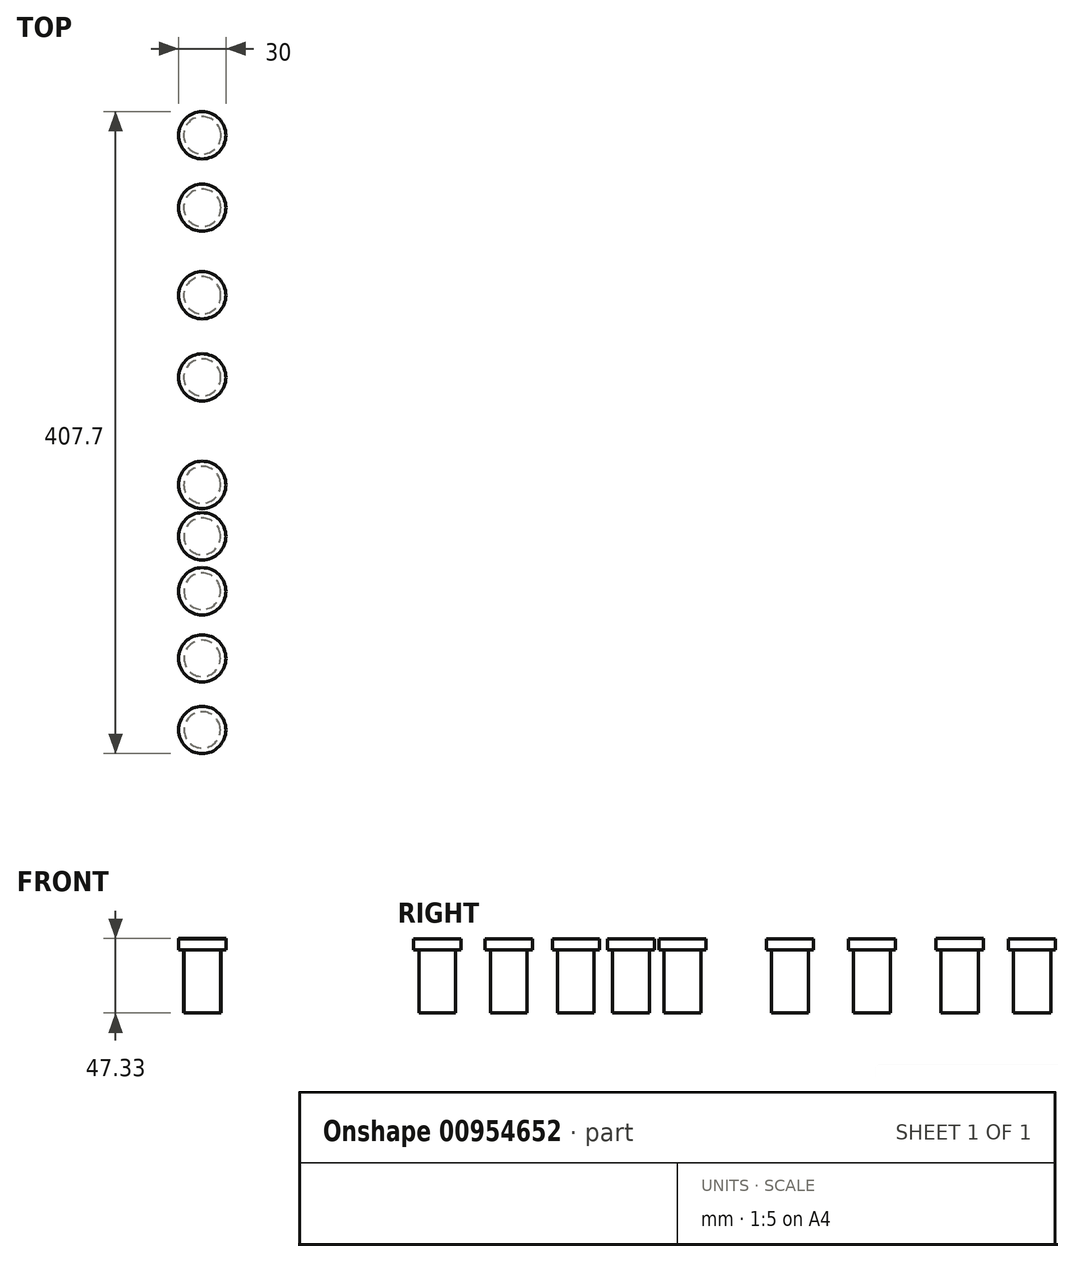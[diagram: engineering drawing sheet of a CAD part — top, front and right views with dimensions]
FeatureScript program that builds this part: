
annotation { "Feature Type Name" : "Feature", "Feature Type Description" : "" }
export const myFeature = defineFeature(function(context is Context, id is Id, definition is map)
    precondition{}
    {
        {
            var Q0;
            Q0=qCreatedBy(makeId("Right.planeOp"),FACE);
            var sketch = newSketch(context, id + "F0", { "sketchPlane" : qUnion([Q0])});
            skLineSegment(sketch, "E0.bottom", {"start": v(0, 0) * mm, "end": v(11.7, 0) * mm});
            skLineSegment(sketch, "E0.top", {"start": v(0, 47) * mm, "end": v(11.7, 47) * mm});
            skLineSegment(sketch, "E0.left", {"start": v(0, 0) * mm, "end": v(0, 47) * mm});
            skLineSegment(sketch, "E0.right", {"start": v(11.7, 0) * mm, "end": v(11.7, 47) * mm});
            skLineSegment(sketch, "E1.bottom", {"start": v(0, 47) * mm, "end": v(15, 47) * mm});
            skLineSegment(sketch, "E1.top", {"start": v(0, 40) * mm, "end": v(15, 40) * mm});
            skLineSegment(sketch, "E1.left", {"start": v(0, 40) * mm, "end": v(0, 47) * mm});
            skLineSegment(sketch, "E1.right", {"start": v(15, 40) * mm, "end": v(15, 47) * mm});
            skLineSegment(sketch, "E2", {"start": v(-171.22, 0) * mm, "end": v(221.99, 0) * mm, "construction": true});
            skLineSegment(sketch, "E3.bottom", {"start": v(-67.64, 0) * mm, "end": v(-79.24, 0) * mm});
            skLineSegment(sketch, "E3.top", {"start": v(-67.64, 40) * mm, "end": v(-79.24, 40) * mm});
            skLineSegment(sketch, "E3.left", {"start": v(-67.64, 0) * mm, "end": v(-67.64, 40) * mm});
            skLineSegment(sketch, "E3.right", {"start": v(-79.24, 0) * mm, "end": v(-79.24, 40) * mm});
            skLineSegment(sketch, "E4.bottom", {"start": v(-67.64, 40) * mm, "end": v(-82.64, 40) * mm});
            skLineSegment(sketch, "E4.top", {"start": v(-67.64, 47) * mm, "end": v(-82.64, 47) * mm});
            skLineSegment(sketch, "E4.left", {"start": v(-67.64, 40) * mm, "end": v(-67.64, 47) * mm});
            skLineSegment(sketch, "E4.right", {"start": v(-82.64, 40) * mm, "end": v(-82.64, 47) * mm});
            skLineSegment(sketch, "E5.bottom", {"start": v(-110.27, 0) * mm, "end": v(-121.82, 0) * mm});
            skLineSegment(sketch, "E5.top", {"start": v(-110.27, 40) * mm, "end": v(-121.82, 40) * mm});
            skLineSegment(sketch, "E5.left", {"start": v(-110.27, 0) * mm, "end": v(-110.27, 40) * mm});
            skLineSegment(sketch, "E5.right", {"start": v(-121.82, 0) * mm, "end": v(-121.82, 40) * mm});
            skLineSegment(sketch, "E6.bottom", {"start": v(-110.27, 40) * mm, "end": v(-125.27, 40) * mm});
            skLineSegment(sketch, "E6.top", {"start": v(-110.27, 47) * mm, "end": v(-125.27, 47) * mm});
            skLineSegment(sketch, "E6.left", {"start": v(-110.27, 40) * mm, "end": v(-110.27, 47) * mm});
            skLineSegment(sketch, "E6.right", {"start": v(-125.27, 40) * mm, "end": v(-125.27, 47) * mm});
            skLineSegment(sketch, "E7.bottom", {"start": v(-155.71, 0) * mm, "end": v(-167.21, 0) * mm});
            skLineSegment(sketch, "E7.top", {"start": v(-155.71, 40) * mm, "end": v(-167.21, 40) * mm});
            skLineSegment(sketch, "E7.left", {"start": v(-155.71, 0) * mm, "end": v(-155.71, 40) * mm});
            skLineSegment(sketch, "E7.right", {"start": v(-167.21, 0) * mm, "end": v(-167.21, 40) * mm});
            skLineSegment(sketch, "E8.bottom", {"start": v(-155.71, 40) * mm, "end": v(-170.71, 40) * mm});
            skLineSegment(sketch, "E8.top", {"start": v(-155.71, 47) * mm, "end": v(-170.71, 47) * mm});
            skLineSegment(sketch, "E8.left", {"start": v(-155.71, 40) * mm, "end": v(-155.71, 47) * mm});
            skLineSegment(sketch, "E8.right", {"start": v(-170.71, 40) * mm, "end": v(-170.71, 47) * mm});
            skLineSegment(sketch, "E9.bottom", {"start": v(221.99, 0) * mm, "end": v(210.09, 0) * mm});
            skLineSegment(sketch, "E9.top", {"start": v(221.99, 40) * mm, "end": v(210.09, 40) * mm});
            skLineSegment(sketch, "E9.left", {"start": v(221.99, 0) * mm, "end": v(221.99, 40) * mm});
            skLineSegment(sketch, "E9.right", {"start": v(210.09, 0) * mm, "end": v(210.09, 40) * mm});
            skLineSegment(sketch, "E10.bottom", {"start": v(221.99, 40) * mm, "end": v(206.99, 40) * mm});
            skLineSegment(sketch, "E10.top", {"start": v(221.99, 47) * mm, "end": v(206.99, 47) * mm});
            skLineSegment(sketch, "E10.left", {"start": v(221.99, 40) * mm, "end": v(221.99, 47) * mm});
            skLineSegment(sketch, "E10.right", {"start": v(206.99, 40) * mm, "end": v(206.99, 47) * mm});
            skLineSegment(sketch, "E11.bottom", {"start": v(120.39, 0) * mm, "end": v(108.59, 0) * mm});
            skLineSegment(sketch, "E11.top", {"start": v(120.39, 40) * mm, "end": v(108.59, 40) * mm});
            skLineSegment(sketch, "E11.left", {"start": v(120.39, 0) * mm, "end": v(120.39, 40) * mm});
            skLineSegment(sketch, "E11.right", {"start": v(108.59, 0) * mm, "end": v(108.59, 40) * mm});
            skLineSegment(sketch, "E12.bottom", {"start": v(120.39, 40) * mm, "end": v(105.39, 40) * mm});
            skLineSegment(sketch, "E12.top", {"start": v(120.39, 47) * mm, "end": v(105.39, 47) * mm});
            skLineSegment(sketch, "E12.left", {"start": v(120.39, 40) * mm, "end": v(120.39, 47) * mm});
            skLineSegment(sketch, "E12.right", {"start": v(105.39, 40) * mm, "end": v(105.39, 47) * mm});
            skLineSegment(sketch, "E13.bottom", {"start": v(68.23, 0) * mm, "end": v(56.48, 0) * mm});
            skLineSegment(sketch, "E13.top", {"start": v(68.23, 40) * mm, "end": v(56.48, 40) * mm});
            skLineSegment(sketch, "E13.left", {"start": v(68.23, 0) * mm, "end": v(68.23, 40) * mm});
            skLineSegment(sketch, "E13.right", {"start": v(56.48, 0) * mm, "end": v(56.48, 40) * mm});
            skLineSegment(sketch, "E14.bottom", {"start": v(68.23, 40) * mm, "end": v(53.23, 40) * mm});
            skLineSegment(sketch, "E14.top", {"start": v(68.23, 47) * mm, "end": v(53.23, 47) * mm});
            skLineSegment(sketch, "E14.left", {"start": v(68.23, 40) * mm, "end": v(68.23, 47) * mm});
            skLineSegment(sketch, "E14.right", {"start": v(53.23, 40) * mm, "end": v(53.23, 47) * mm});
            skLineSegment(sketch, "E15.bottom", {"start": v(-32.72, 0) * mm, "end": v(-44.37, 0) * mm});
            skLineSegment(sketch, "E15.top", {"start": v(-32.72, 40) * mm, "end": v(-44.37, 40) * mm});
            skLineSegment(sketch, "E15.left", {"start": v(-32.72, 0) * mm, "end": v(-32.72, 40) * mm});
            skLineSegment(sketch, "E15.right", {"start": v(-44.37, 0) * mm, "end": v(-44.37, 40) * mm});
            skLineSegment(sketch, "E16.bottom", {"start": v(-32.72, 40) * mm, "end": v(-47.72, 40) * mm});
            skLineSegment(sketch, "E16.top", {"start": v(-32.72, 47) * mm, "end": v(-47.72, 47) * mm});
            skLineSegment(sketch, "E16.left", {"start": v(-32.72, 40) * mm, "end": v(-32.72, 47) * mm});
            skLineSegment(sketch, "E16.right", {"start": v(-47.72, 40) * mm, "end": v(-47.72, 47) * mm});
            skLineSegment(sketch, "E17.bottom", {"start": v(164.15, 0) * mm, "end": v(176, 0) * mm});
            skLineSegment(sketch, "E17.top", {"start": v(164.15, 40) * mm, "end": v(176, 40) * mm});
            skLineSegment(sketch, "E17.left", {"start": v(164.15, 0) * mm, "end": v(164.15, 40) * mm});
            skLineSegment(sketch, "E17.right", {"start": v(176, 0) * mm, "end": v(176, 40) * mm});
            skLineSegment(sketch, "E18.bottom", {"start": v(176, 40) * mm, "end": v(161, 40) * mm});
            skLineSegment(sketch, "E18.top", {"start": v(176, 47.33) * mm, "end": v(161, 47.33) * mm});
            skLineSegment(sketch, "E18.left", {"start": v(176, 40) * mm, "end": v(176, 47.33) * mm});
            skLineSegment(sketch, "E18.right", {"start": v(161, 40) * mm, "end": v(161, 47.33) * mm});
            skSolve(sketch);
        }
        {
            var Q0;
            {var subQ0=sQuery(id+"F0.wireOp",EDGE,"E0.top");Q0=makeQuery(id+"F0.imprint","IMPRINT",FACE,{"disambiguationData":[TD([[makeQuery(id+"F0.imprint","IMPRINT",EDGE,{"derivedFrom":subQ0}),-1.0]])]});}
            var Q1;
            {var subQ0=sQuery(id+"F0.wireOp",EDGE,"E1.bottom");Q1=makeQuery(id+"F0.imprint","IMPRINT",FACE,{"disambiguationData":[TD([[makeQuery(id+"F0.imprint","IMPRINT",EDGE,{"derivedFrom":subQ0}),-1.0]])]});}
            var Q2;
            {var subQ0=sQuery(id+"F0.wireOp",EDGE,"E0.bottom");Q2=makeQuery(id+"F0.imprint","IMPRINT",FACE,{"disambiguationData":[TD([[makeQuery(id+"F0.imprint","IMPRINT",EDGE,{"derivedFrom":subQ0}),1.0]])]});}
            var Q3;
            Q3=sQuery(id+"F0.wireOp",EDGE,"E0.left");
            revolve(context, id + "F1", {"surfaceOperationType" : NewSurfaceOperationType.NEW, "entities" : qUnion([Q0, Q1, Q2]), "axis" : qUnion([Q3]), "revolveType" : RevolveType.FULL});
        }
        {
            var Q0;
            Q0=makeQuery(id+"F0.imprint","IMPRINT",FACE,{"disambiguationData":[TD([[makeQuery(id+"F0.imprint","IMPRINT",EDGE,{"derivedFrom":sQuery(id+"F0.wireOp",EDGE,"E9.bottom")}),-1.0]])]});
            var Q1;
            Q1=makeQuery(id+"F0.imprint","IMPRINT",FACE,{"disambiguationData":[TD([[makeQuery(id+"F0.imprint","IMPRINT",EDGE,{"derivedFrom":sQuery(id+"F0.wireOp",EDGE,"E9.top")}),-1.0]])]});
            var Q2;
            Q2=sQuery(id+"F0.wireOp",EDGE,"E9.left");
            revolve(context, id + "F2", {"surfaceOperationType" : NewSurfaceOperationType.NEW, "entities" : qUnion([Q0, Q1]), "axis" : qUnion([Q2]), "revolveType" : RevolveType.FULL});
        }
        {
            var Q0;
            Q0=makeQuery(id+"F0.imprint","IMPRINT",FACE,{"disambiguationData":[TD([[makeQuery(id+"F0.imprint","IMPRINT",EDGE,{"derivedFrom":sQuery(id+"F0.wireOp",EDGE,"E17.bottom")}),1.0]])]});
            var Q1;
            Q1=makeQuery(id+"F0.imprint","IMPRINT",FACE,{"disambiguationData":[TD([[makeQuery(id+"F0.imprint","IMPRINT",EDGE,{"derivedFrom":sQuery(id+"F0.wireOp",EDGE,"E17.top")}),1.0]])]});
            var Q2;
            Q2=sQuery(id+"F0.wireOp",EDGE,"E17.right");
            revolve(context, id + "F3", {"surfaceOperationType" : NewSurfaceOperationType.NEW, "entities" : qUnion([Q0, Q1]), "axis" : qUnion([Q2]), "revolveType" : RevolveType.FULL});
        }
        {
            var Q0;
            Q0=makeQuery(id+"F0.imprint","IMPRINT",FACE,{"disambiguationData":[TD([[makeQuery(id+"F0.imprint","IMPRINT",EDGE,{"derivedFrom":sQuery(id+"F0.wireOp",EDGE,"E11.bottom")}),-1.0]])]});
            var Q1;
            Q1=makeQuery(id+"F0.imprint","IMPRINT",FACE,{"disambiguationData":[TD([[makeQuery(id+"F0.imprint","IMPRINT",EDGE,{"derivedFrom":sQuery(id+"F0.wireOp",EDGE,"E11.top")}),-1.0]])]});
            var Q2;
            Q2=sQuery(id+"F0.wireOp",EDGE,"E11.left");
            revolve(context, id + "F4", {"surfaceOperationType" : NewSurfaceOperationType.NEW, "entities" : qUnion([Q0, Q1]), "axis" : qUnion([Q2]), "revolveType" : RevolveType.FULL});
        }
        {
            var Q0;
            Q0=makeQuery(id+"F0.imprint","IMPRINT",FACE,{"disambiguationData":[TD([[makeQuery(id+"F0.imprint","IMPRINT",EDGE,{"derivedFrom":sQuery(id+"F0.wireOp",EDGE,"E13.top")}),-1.0]])]});
            var Q1;
            Q1=makeQuery(id+"F0.imprint","IMPRINT",FACE,{"disambiguationData":[TD([[makeQuery(id+"F0.imprint","IMPRINT",EDGE,{"derivedFrom":sQuery(id+"F0.wireOp",EDGE,"E13.bottom")}),-1.0]])]});
            var Q2;
            Q2=sQuery(id+"F0.wireOp",EDGE,"E13.left");
            revolve(context, id + "F5", {"surfaceOperationType" : NewSurfaceOperationType.NEW, "entities" : qUnion([Q0, Q1]), "axis" : qUnion([Q2]), "revolveType" : RevolveType.FULL});
        }
        {
            var Q0;
            Q0=makeQuery(id+"F0.imprint","IMPRINT",FACE,{"disambiguationData":[TD([[makeQuery(id+"F0.imprint","IMPRINT",EDGE,{"derivedFrom":sQuery(id+"F0.wireOp",EDGE,"E15.bottom")}),-1.0]])]});
            var Q1;
            Q1=makeQuery(id+"F0.imprint","IMPRINT",FACE,{"disambiguationData":[TD([[makeQuery(id+"F0.imprint","IMPRINT",EDGE,{"derivedFrom":sQuery(id+"F0.wireOp",EDGE,"E15.top")}),-1.0]])]});
            var Q2;
            Q2=sQuery(id+"F0.wireOp",EDGE,"E15.left");
            revolve(context, id + "F6", {"surfaceOperationType" : NewSurfaceOperationType.NEW, "entities" : qUnion([Q0, Q1]), "axis" : qUnion([Q2]), "revolveType" : RevolveType.FULL});
        }
        {
            var Q0;
            Q0=makeQuery(id+"F0.imprint","IMPRINT",FACE,{"disambiguationData":[TD([[makeQuery(id+"F0.imprint","IMPRINT",EDGE,{"derivedFrom":sQuery(id+"F0.wireOp",EDGE,"E3.top")}),-1.0]])]});
            var Q1;
            Q1=makeQuery(id+"F0.imprint","IMPRINT",FACE,{"disambiguationData":[TD([[makeQuery(id+"F0.imprint","IMPRINT",EDGE,{"derivedFrom":sQuery(id+"F0.wireOp",EDGE,"E3.bottom")}),-1.0]])]});
            var Q2;
            Q2=sQuery(id+"F0.wireOp",EDGE,"E3.left");
            revolve(context, id + "F7", {"surfaceOperationType" : NewSurfaceOperationType.NEW, "entities" : qUnion([Q0, Q1]), "axis" : qUnion([Q2]), "revolveType" : RevolveType.FULL});
        }
        {
            var Q0;
            Q0=makeQuery(id+"F0.imprint","IMPRINT",FACE,{"disambiguationData":[TD([[makeQuery(id+"F0.imprint","IMPRINT",EDGE,{"derivedFrom":sQuery(id+"F0.wireOp",EDGE,"E5.bottom")}),-1.0]])]});
            var Q1;
            Q1=makeQuery(id+"F0.imprint","IMPRINT",FACE,{"disambiguationData":[TD([[makeQuery(id+"F0.imprint","IMPRINT",EDGE,{"derivedFrom":sQuery(id+"F0.wireOp",EDGE,"E5.top")}),-1.0]])]});
            var Q2;
            Q2=sQuery(id+"F0.wireOp",EDGE,"E5.left");
            revolve(context, id + "F8", {"surfaceOperationType" : NewSurfaceOperationType.NEW, "entities" : qUnion([Q0, Q1]), "axis" : qUnion([Q2]), "revolveType" : RevolveType.FULL});
        }
        {
            var Q0;
            Q0=makeQuery(id+"F0.imprint","IMPRINT",FACE,{"disambiguationData":[TD([[makeQuery(id+"F0.imprint","IMPRINT",EDGE,{"derivedFrom":sQuery(id+"F0.wireOp",EDGE,"E7.top")}),-1.0]])]});
            var Q1;
            Q1=makeQuery(id+"F0.imprint","IMPRINT",FACE,{"disambiguationData":[TD([[makeQuery(id+"F0.imprint","IMPRINT",EDGE,{"derivedFrom":sQuery(id+"F0.wireOp",EDGE,"E7.bottom")}),-1.0]])]});
            var Q2;
            Q2=sQuery(id+"F0.wireOp",EDGE,"E7.left");
            revolve(context, id + "F9", {"surfaceOperationType" : NewSurfaceOperationType.NEW, "entities" : qUnion([Q0, Q1]), "axis" : qUnion([Q2]), "revolveType" : RevolveType.FULL});
        }
    });
